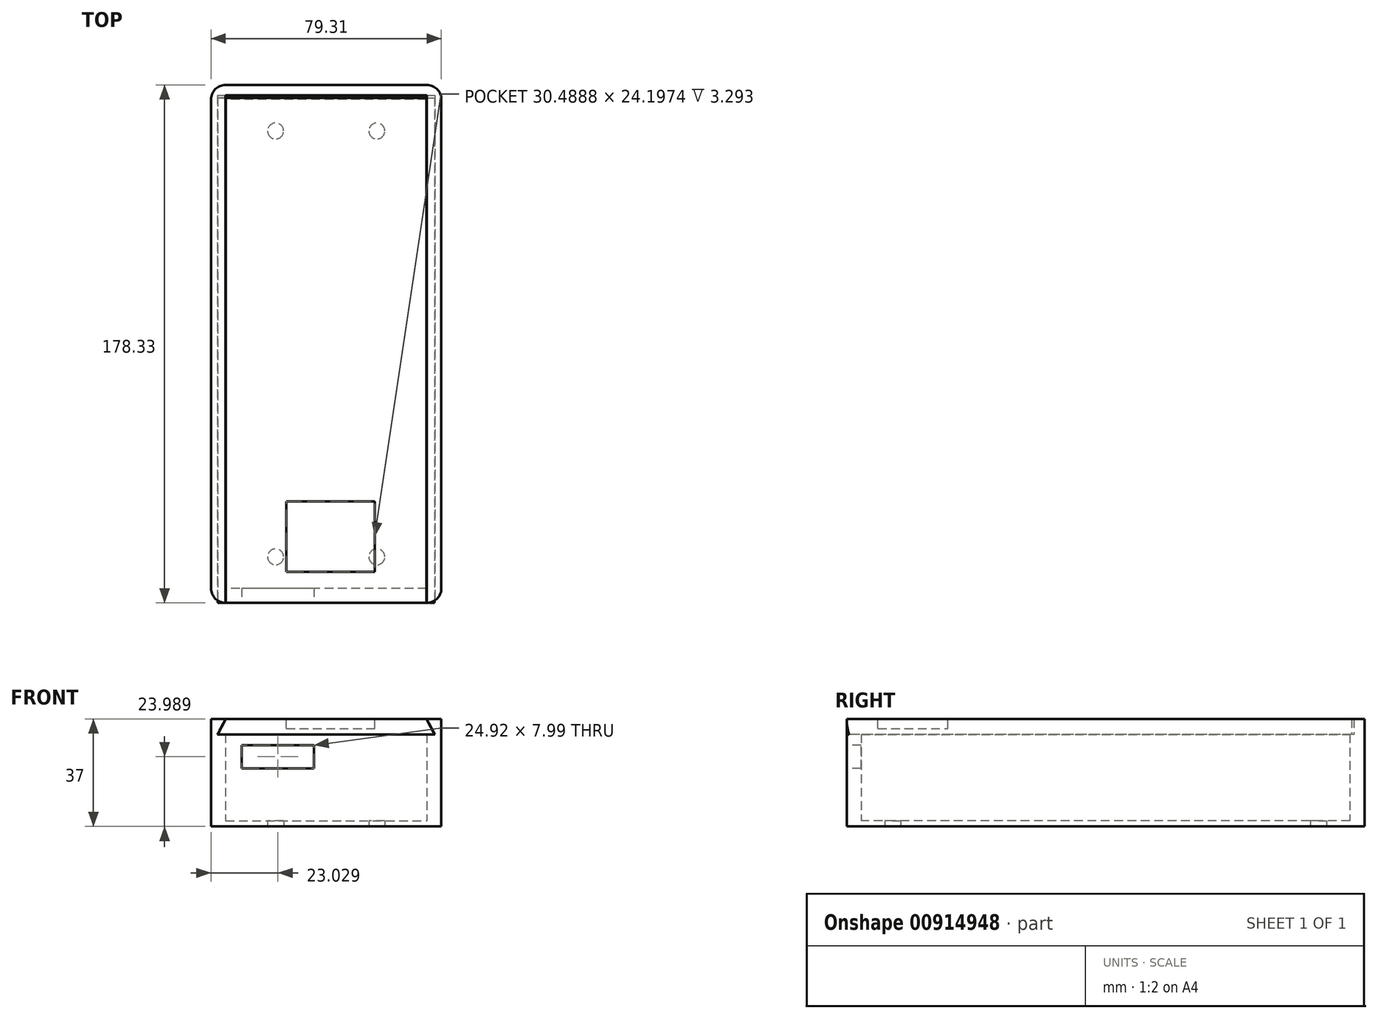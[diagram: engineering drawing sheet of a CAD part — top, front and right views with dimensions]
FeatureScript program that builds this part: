
annotation { "Feature Type Name" : "Feature", "Feature Type Description" : "" }
export const myFeature = defineFeature(function(context is Context, id is Id, definition is map)
    precondition{}
    {
        {
            var Q0;
            Q0=qCreatedBy(makeId("Top.planeOp"),FACE);
            var sketch = newSketch(context, id + "F0", { "sketchPlane" : qUnion([Q0])});
            skLineSegment(sketch, "E0.bottom", {"start": v(-54.92, 26.7) * mm, "end": v(14.4, 26.7) * mm});
            skLineSegment(sketch, "E0.top", {"start": v(-54.92, -141.62) * mm, "end": v(14.4, -141.62) * mm});
            skLineSegment(sketch, "E0.left", {"start": v(-54.92, 26.7) * mm, "end": v(-54.92, -141.62) * mm});
            skLineSegment(sketch, "E0.right", {"start": v(14.4, 26.7) * mm, "end": v(14.4, -141.62) * mm});
            skLineSegment(sketch, "E1.0", {"start": v(-54.92, 31.7) * mm, "end": v(14.4, 31.7) * mm});
            skLineSegment(sketch, "E1.1", {"start": v(-59.92, 26.7) * mm, "end": v(-59.92, -141.62) * mm});
            skLineSegment(sketch, "E1.2", {"start": v(-54.92, -146.62) * mm, "end": v(14.4, -146.62) * mm});
            skLineSegment(sketch, "E1.3", {"start": v(19.4, 26.7) * mm, "end": v(19.4, -141.62) * mm});
            skPoint(sketch, "E2.visualSharp", {"position": v(-59.92, 31.7) * mm});
            skArc(sketch, "E2.filletArc", {"start": v(-54.92, 31.7) * mm, "mid": v(-58.46, 30.24) * mm, "end": v(-59.92, 26.7) * mm});
            skPoint(sketch, "E3.visualSharp", {"position": v(19.4, 31.7) * mm});
            skArc(sketch, "E3.filletArc", {"start": v(19.4, 26.7) * mm, "mid": v(17.93, 30.24) * mm, "end": v(14.4, 31.7) * mm});
            skPoint(sketch, "E4.visualSharp", {"position": v(-59.92, -146.62) * mm});
            skArc(sketch, "E4.filletArc", {"start": v(-59.92, -141.62) * mm, "mid": v(-58.46, -145.15) * mm, "end": v(-54.92, -146.62) * mm});
            skPoint(sketch, "E5.visualSharp", {"position": v(19.4, -146.62) * mm});
            skArc(sketch, "E5.filletArc", {"start": v(14.4, -146.62) * mm, "mid": v(17.93, -145.15) * mm, "end": v(19.4, -141.62) * mm});
            skSolve(sketch);
        }
        {
            var Q0;
            Q0 = qSketchRegion(id + "F0", true);
            var Q1;
            Q1=makeQuery(id+"F0.imprint","IMPRINT",FACE,{"disambiguationData":[TD([[makeQuery(id+"F0.imprint","IMPRINT",EDGE,{"derivedFrom":sQuery(id+"F0.wireOp",EDGE,"E0.bottom")}),-1.0]])]});
            extrude(context, id + "F1", {"entities" : qUnion([Q0, Q1]), "oppositeDirection" : true, "depth" : 2 * mm, "offsetDistance" : 25 * mm});
        }
        {
            var Q0;
            Q0=makeQuery(id+"F0.imprint","IMPRINT",FACE,{"disambiguationData":[TD([[makeQuery(id+"F0.imprint","IMPRINT",EDGE,{"derivedFrom":sQuery(id+"F0.wireOp",EDGE,"E0.bottom")}),1.0]])]});
            extrude(context, id + "F2", {"entities" : qUnion([Q0]), "operationType" : NewBodyOperationType.ADD, "depth" : 35 * mm, "offsetDistance" : 25 * mm});
        }
        {
            var Q0;
            {var subQ0=sQuery(id+"F0.wireOp",EDGE,"E1.2");Q0=makeQuery(id+"F2.boolean.opBoolean","MERGE",FACE,{"derivedFrom":[makeQuery(id+"F1.opExtrude","SWEPT_FACE",FACE,{"disambiguationData":[OSD([subQ0])]}),makeQuery(id+"F2.opExtrude","SWEPT_FACE",FACE,{"disambiguationData":[OSD([subQ0])]})]});}
            var sketch = newSketch(context, id + "F3", { "sketchPlane" : qUnion([Q0])});
            skLineSegment(sketch, "E6.bottom", {"start": v(-49.35, 25.99) * mm, "end": v(-24.43, 25.99) * mm});
            skLineSegment(sketch, "E6.top", {"start": v(-49.35, 18) * mm, "end": v(-24.43, 18) * mm});
            skLineSegment(sketch, "E6.left", {"start": v(-49.35, 25.99) * mm, "end": v(-49.35, 18) * mm});
            skLineSegment(sketch, "E6.right", {"start": v(-24.43, 25.99) * mm, "end": v(-24.43, 18) * mm});
            skSolve(sketch);
        }
        {
            var Q0;
            Q0 = qSketchRegion(id + "F3", true);
            extrude(context, id + "F4", {"entities" : qUnion([Q0]), "operationType" : NewBodyOperationType.REMOVE, "oppositeDirection" : true, "depth" : 25 * mm, "offsetDistance" : 25 * mm});
        }
        {
            var Q0;
            {var subQ0=sQuery(id+"F0.wireOp",EDGE,"E1.2");Q0=makeQuery(id+"F2.boolean.opBoolean","MERGE",FACE,{"derivedFrom":[makeQuery(id+"F1.opExtrude","SWEPT_FACE",FACE,{"disambiguationData":[OSD([subQ0])]}),makeQuery(id+"F2.opExtrude","SWEPT_FACE",FACE,{"disambiguationData":[OSD([subQ0])]})]});}
            var sketch = newSketch(context, id + "F5", { "sketchPlane" : qUnion([Q0])});
            skLineSegment(sketch, "E7.0.0", {"start": v(14.4, -2) * mm, "end": v(14.4, 35) * mm});
            skLineSegment(sketch, "E7.0.1", {"start": v(14.4, 35) * mm, "end": v(-54.92, 35) * mm});
            skLineSegment(sketch, "E7.0.2", {"start": v(-54.92, 35) * mm, "end": v(-54.92, -2) * mm});
            skLineSegment(sketch, "E7.0.3", {"start": v(-54.92, -2) * mm, "end": v(14.4, -2) * mm});
            skLineSegment(sketch, "E8.0.0", {"start": v(-54.92, -2) * mm, "end": v(-54.92, 35) * mm});
            skLineSegment(sketch, "E8.0.1", {"start": v(-54.92, 35) * mm, "end": v(-59.92, 35) * mm});
            skLineSegment(sketch, "E8.0.2", {"start": v(-59.92, 35) * mm, "end": v(-59.92, -2) * mm});
            skLineSegment(sketch, "E8.0.3", {"start": v(-59.92, -2) * mm, "end": v(-54.92, -2) * mm});
            skLineSegment(sketch, "E9.0.0", {"start": v(19.4, -2) * mm, "end": v(19.4, 35) * mm});
            skLineSegment(sketch, "E9.0.1", {"start": v(19.4, 35) * mm, "end": v(14.4, 35) * mm});
            skLineSegment(sketch, "E9.0.2", {"start": v(14.4, 35) * mm, "end": v(14.4, -2) * mm});
            skLineSegment(sketch, "E9.0.3", {"start": v(14.4, -2) * mm, "end": v(19.4, -2) * mm});
            skLineSegment(sketch, "E10", {"start": v(-54.92, 35) * mm, "end": v(-57.72, 29.7) * mm});
            skLineSegment(sketch, "E11", {"start": v(-57.72, 29.7) * mm, "end": v(-54.92, 29.7) * mm});
            skLineSegment(sketch, "E12", {"start": v(-54.92, 29.7) * mm, "end": v(14.4, 29.7) * mm});
            skLineSegment(sketch, "E13", {"start": v(14.4, 35) * mm, "end": v(17.2, 29.7) * mm});
            skLineSegment(sketch, "E14", {"start": v(17.2, 29.7) * mm, "end": v(14.4, 29.7) * mm});
            skSolve(sketch);
        }
        {
            var Q0;
            {var subQ0=sQuery(id+"F5.wireOp",EDGE,"E10");Q0=makeQuery(id+"F5.imprint","IMPRINT",FACE,{"disambiguationData":[TD([[makeQuery(id+"F5.imprint","IMPRINT",EDGE,{"derivedFrom":subQ0}),1.0]])]});}
            var Q1;
            {var subQ0=sQuery(id+"F5.wireOp",EDGE,"E7.0.1");Q1=makeQuery(id+"F5.imprint","IMPRINT",FACE,{"disambiguationData":[TD([[makeQuery(id+"F5.imprint","IMPRINT",EDGE,{"derivedFrom":subQ0}),-1.0]])]});}
            var Q2;
            {var subQ0=sQuery(id+"F5.wireOp",EDGE,"E13");Q2=makeQuery(id+"F5.imprint","IMPRINT",FACE,{"disambiguationData":[TD([[makeQuery(id+"F5.imprint","IMPRINT",EDGE,{"derivedFrom":subQ0}),-1.0]])]});}
            extrude(context, id + "F6", {"entities" : qUnion([Q0, Q1, Q2]), "operationType" : NewBodyOperationType.REMOVE, "oppositeDirection" : true, "depth" : 174.7 * mm, "offsetDistance" : 25 * mm});
        }
        {
            var Q0;
            {var subQ0=sQuery(id+"F5.wireOp",EDGE,"E7.0.1");Q0=makeQuery(id+"F5.imprint","IMPRINT",FACE,{"disambiguationData":[TD([[makeQuery(id+"F5.imprint","IMPRINT",EDGE,{"derivedFrom":subQ0}),-1.0]])]});}
            var Q1;
            {var subQ0=sQuery(id+"F5.wireOp",EDGE,"E10");Q1=makeQuery(id+"F5.imprint","IMPRINT",FACE,{"disambiguationData":[TD([[makeQuery(id+"F5.imprint","IMPRINT",EDGE,{"derivedFrom":subQ0}),1.0]])]});}
            var Q2;
            {var subQ0=sQuery(id+"F5.wireOp",EDGE,"E13");Q2=makeQuery(id+"F5.imprint","IMPRINT",FACE,{"disambiguationData":[TD([[makeQuery(id+"F5.imprint","IMPRINT",EDGE,{"derivedFrom":subQ0}),-1.0]])]});}
            extrude(context, id + "F7", {"entities" : qUnion([Q0, Q1, Q2]), "oppositeDirection" : true, "depth" : 174.2 * mm, "offsetDistance" : 25 * mm});
        }
        {
            var Q0;
            Q0=makeQuery(id+"F7.opExtrude","SWEPT_FACE",FACE,{"disambiguationData":[OSD([sQuery(id+"F5.wireOp",EDGE,"E7.0.1")])]});
            var sketch = newSketch(context, id + "F8", { "sketchPlane" : qUnion([Q0])});
            skLineSegment(sketch, "E15.bottom", {"start": v(-34, -135.96) * mm, "end": v(-3.45, -135.96) * mm});
            skLineSegment(sketch, "E15.top", {"start": v(-34, -111.71) * mm, "end": v(-3.45, -111.71) * mm});
            skLineSegment(sketch, "E15.left", {"start": v(-34, -135.96) * mm, "end": v(-34, -111.71) * mm});
            skLineSegment(sketch, "E15.right", {"start": v(-3.45, -135.96) * mm, "end": v(-3.45, -111.71) * mm});
            skSolve(sketch);
        }
        {
            var Q0;
            Q0 = qSketchRegion(id + "F8", true);
            extrude(context, id + "F9", {"entities" : qUnion([Q0]), "operationType" : NewBodyOperationType.REMOVE, "oppositeDirection" : true, "depth" : 3.3 * mm, "offsetDistance" : 25 * mm});
        }
        {
            var Q0;
            Q0=makeQuery(id+"F7.opExtrude","SWEPT_BODY",BODY,{"disambiguationData":[OSD([sQuery(id+"F5.wireOp",EDGE,"E7.0.1"),sQuery(id+"F5.wireOp",EDGE,"E10"),sQuery(id+"F5.wireOp",EDGE,"E11"),sQuery(id+"F5.wireOp",EDGE,"E12"),sQuery(id+"F5.wireOp",EDGE,"E13"),sQuery(id+"F5.wireOp",EDGE,"E14")])]});
            var Q1;
            Q1=makeQuery(id+"F9.boolean.opBoolean","COPY",VERTEX,{"derivedFrom":makeQuery(id+"F9.opExtrude","CAP_VERTEX",VERTEX,{"disambiguationData":[OSD([sQuery(id+"F8.wireOp",EDGE,"E15.top"),sQuery(id+"F8.wireOp",EDGE,"E15.left")])],"isStart":true})});
            var Q2;
            Q2=makeQuery(id+"F9.boolean.opBoolean","COPY",VERTEX,{"derivedFrom":makeQuery(id+"F9.opExtrude","CAP_VERTEX",VERTEX,{"disambiguationData":[OSD([sQuery(id+"F8.wireOp",EDGE,"E15.top"),sQuery(id+"F8.wireOp",EDGE,"E15.left")])],"isStart":true})});
            transform(context, id + "F10", {"entities" : qUnion([Q0]), "transformType" : TransformType.SCALE_UNIFORMLY, "scale" : 1, "scalePoint" : qUnion([Q2]), "makeCopy" : false});
        }
        {
            var Q0;
            Q0=makeQuery(id+"F1.opExtrude","CAP_FACE",FACE,{"disambiguationData":[OSD([sQuery(id+"F0.wireOp",EDGE,"E1.0"),sQuery(id+"F0.wireOp",EDGE,"E1.1"),sQuery(id+"F0.wireOp",EDGE,"E1.2"),sQuery(id+"F0.wireOp",EDGE,"E1.3"),sQuery(id+"F0.wireOp",EDGE,"E2.filletArc"),sQuery(id+"F0.wireOp",EDGE,"E3.filletArc"),sQuery(id+"F0.wireOp",EDGE,"E4.filletArc"),sQuery(id+"F0.wireOp",EDGE,"E5.filletArc")])],"isStart":false});
            var sketch = newSketch(context, id + "F11", { "sketchPlane" : qUnion([Q0])});
            skArc(sketch, "E16.0.0", {"start": v(-54.92, 146.62) * mm, "mid": v(-58.46, 145.15) * mm, "end": v(-59.92, 141.62) * mm});
            skLineSegment(sketch, "E16.0.1", {"start": v(-59.92, 141.62) * mm, "end": v(-59.92, -26.7) * mm});
            skArc(sketch, "E16.0.2", {"start": v(-59.92, -26.7) * mm, "mid": v(-58.46, -30.24) * mm, "end": v(-54.92, -31.7) * mm});
            skLineSegment(sketch, "E16.0.3", {"start": v(-54.92, -31.7) * mm, "end": v(14.4, -31.7) * mm});
            skArc(sketch, "E16.0.4", {"start": v(14.4, -31.7) * mm, "mid": v(17.93, -30.24) * mm, "end": v(19.4, -26.7) * mm});
            skLineSegment(sketch, "E16.0.5", {"start": v(19.4, -26.7) * mm, "end": v(19.4, 141.62) * mm});
            skArc(sketch, "E16.0.6", {"start": v(19.4, 141.62) * mm, "mid": v(17.93, 145.15) * mm, "end": v(14.4, 146.62) * mm});
            skLineSegment(sketch, "E16.0.7", {"start": v(14.4, 146.62) * mm, "end": v(-54.92, 146.62) * mm});
            skPoint(sketch, "E17.middle", {"position": v(-20.26, 57.45) * mm});
            skCircle(sketch, "E18", {"center": v(-37.7, 130.77) * mm, "radius": 2.75 * mm});
            skCircle(sketch, "E19", {"center": v(-2.82, 130.77) * mm, "radius": 2.75 * mm});
            skCircle(sketch, "E20", {"center": v(-37.7, -15.86) * mm, "radius": 2.75 * mm});
            skCircle(sketch, "E21", {"center": v(-2.82, -15.86) * mm, "radius": 2.75 * mm});
            skSolve(sketch);
        }
        {
            var Q0;
            Q0=makeQuery(id+"F11.imprint","IMPRINT",FACE,{"disambiguationData":[TD([[makeQuery(id+"F11.imprint","IMPRINT",EDGE,{"derivedFrom":sQuery(id+"F11.wireOp",EDGE,"E18")}),1.0]])]});
            var Q1;
            Q1=makeQuery(id+"F11.imprint","IMPRINT",FACE,{"disambiguationData":[TD([[makeQuery(id+"F11.imprint","IMPRINT",EDGE,{"derivedFrom":sQuery(id+"F11.wireOp",EDGE,"E19")}),1.0]])]});
            var Q2;
            Q2=makeQuery(id+"F11.imprint","IMPRINT",FACE,{"disambiguationData":[TD([[makeQuery(id+"F11.imprint","IMPRINT",EDGE,{"derivedFrom":sQuery(id+"F11.wireOp",EDGE,"E20")}),1.0]])]});
            var Q3;
            Q3=makeQuery(id+"F11.imprint","IMPRINT",FACE,{"disambiguationData":[TD([[makeQuery(id+"F11.imprint","IMPRINT",EDGE,{"derivedFrom":sQuery(id+"F11.wireOp",EDGE,"E21")}),1.0]])]});
            extrude(context, id + "F12", {"entities" : qUnion([Q0, Q1, Q2, Q3]), "operationType" : NewBodyOperationType.REMOVE, "oppositeDirection" : true, "depth" : 25 * mm, "offsetDistance" : 25 * mm});
        }
    });
